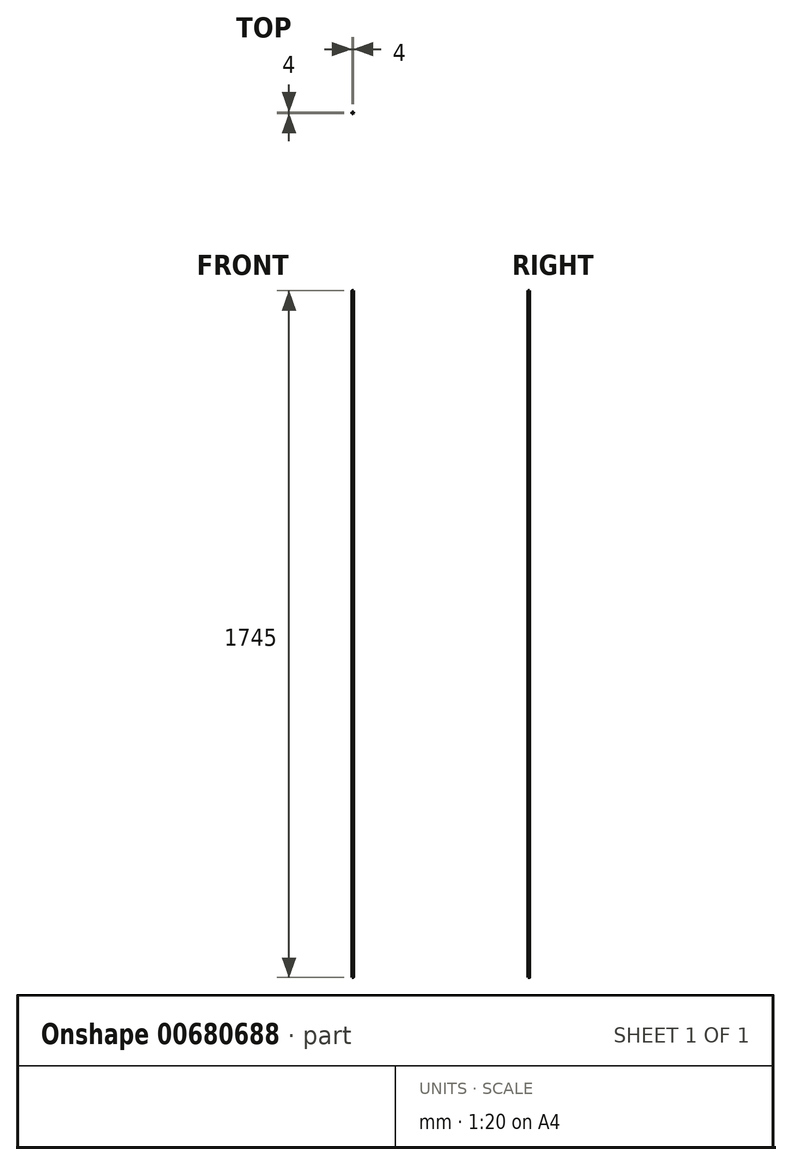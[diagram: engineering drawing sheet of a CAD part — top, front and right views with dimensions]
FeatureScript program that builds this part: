
annotation { "Feature Type Name" : "Feature", "Feature Type Description" : "" }
export const myFeature = defineFeature(function(context is Context, id is Id, definition is map)
    precondition{}
    {
        {
            var Q0;
            Q0=qCreatedBy(makeId("Top.planeOp"),FACE);
            var sketch = newSketch(context, id + "F0", { "sketchPlane" : qUnion([Q0])});
            skCircle(sketch, "E0", {"center": v(0, 0) * mm, "radius": 2 * mm});
            skSolve(sketch);
        }
        {
            var Q0;
            Q0=makeQuery(id+"F0.imprint","IMPRINT",FACE,{"disambiguationData":[TD([[makeQuery(id+"F0.imprint","IMPRINT",EDGE,{"derivedFrom":sQuery(id+"F0.wireOp",EDGE,"E0")}),1.0]])]});
            extrude(context, id + "F1", {"entities" : qUnion([Q0]), "depth" : 1745 * mm, "offsetDistance" : 25 * mm});
        }
    });
